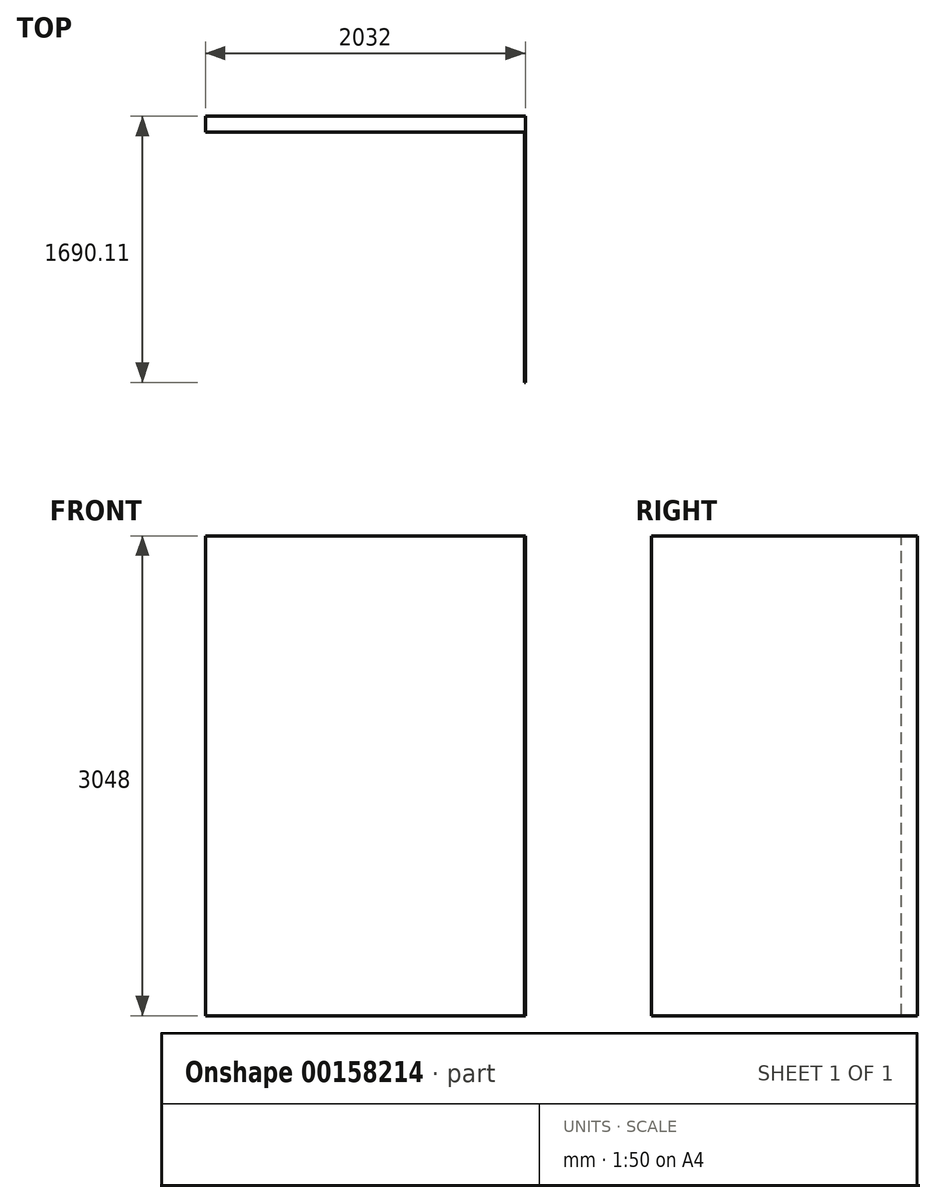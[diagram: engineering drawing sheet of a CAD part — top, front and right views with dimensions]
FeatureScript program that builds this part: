
annotation { "Feature Type Name" : "Feature", "Feature Type Description" : "" }
export const myFeature = defineFeature(function(context is Context, id is Id, definition is map)
    precondition{}
    {
        {
            var Q0;
            Q0=qCreatedBy(makeId("Front.planeOp"),FACE);
            var sketch = newSketch(context, id + "F0", { "sketchPlane" : qUnion([Q0])});
            skLineSegment(sketch, "E0", {"start": v(-2032, 1616.8) * mm, "end": v(-2032, -1431.2) * mm});
            skLineSegment(sketch, "E1", {"start": v(-2032, -1431.2) * mm, "end": v(0, -1431.2) * mm});
            skLineSegment(sketch, "E2", {"start": v(0, -1431.2) * mm, "end": v(0, 1616.8) * mm});
            skLineSegment(sketch, "E3", {"start": v(0, 1616.8) * mm, "end": v(-2032, 1616.8) * mm});
            skSolve(sketch);
        }
        {
            var Q0;
            Q0=makeQuery(id+"F0.imprint","IMPRINT",FACE,{"disambiguationData":[TD([[makeQuery(id+"F0.imprint","IMPRINT",EDGE,{"derivedFrom":sQuery(id+"F0.wireOp",EDGE,"E0")}),1.0]])]});
            extrude(context, id + "F1", {"entities" : qUnion([Q0]), "depth" : 101.6 * mm});
        }
        {
            var Q0;
            Q0=makeQuery(id+"F1.opExtrude","SWEPT_FACE",FACE,{"disambiguationData":[OSD([sQuery(id+"F0.wireOp",EDGE,"E2")])]});
            var sketch = newSketch(context, id + "F2", { "sketchPlane" : qUnion([Q0])});
            skLineSegment(sketch, "E4", {"start": v(0, 1616.8) * mm, "end": v(-1690.1, 1616.8) * mm});
            skLineSegment(sketch, "E5", {"start": v(-1690.1, 1616.8) * mm, "end": v(-1690.1, -1431.2) * mm});
            skLineSegment(sketch, "E6", {"start": v(-1690.1, -1431.2) * mm, "end": v(-101.6, -1431.2) * mm});
            skSolve(sketch);
        }
        {
            var Q0;
            {var subQ2=sQuery(id+"F2.wireOp",EDGE,"E5");Q0=makeQuery(id+"F2.imprint","IMPRINT",FACE,{"disambiguationData":[TD([[makeQuery(id+"F2.imprint","IMPRINT",EDGE,{"derivedFrom":subQ2}),1.0]])]});}
            extrude(context, id + "F3", {"entities" : qUnion([Q0]), "operationType" : NewBodyOperationType.ADD, "oppositeDirection" : true, "depth" : 4 * mm});
        }
    });
